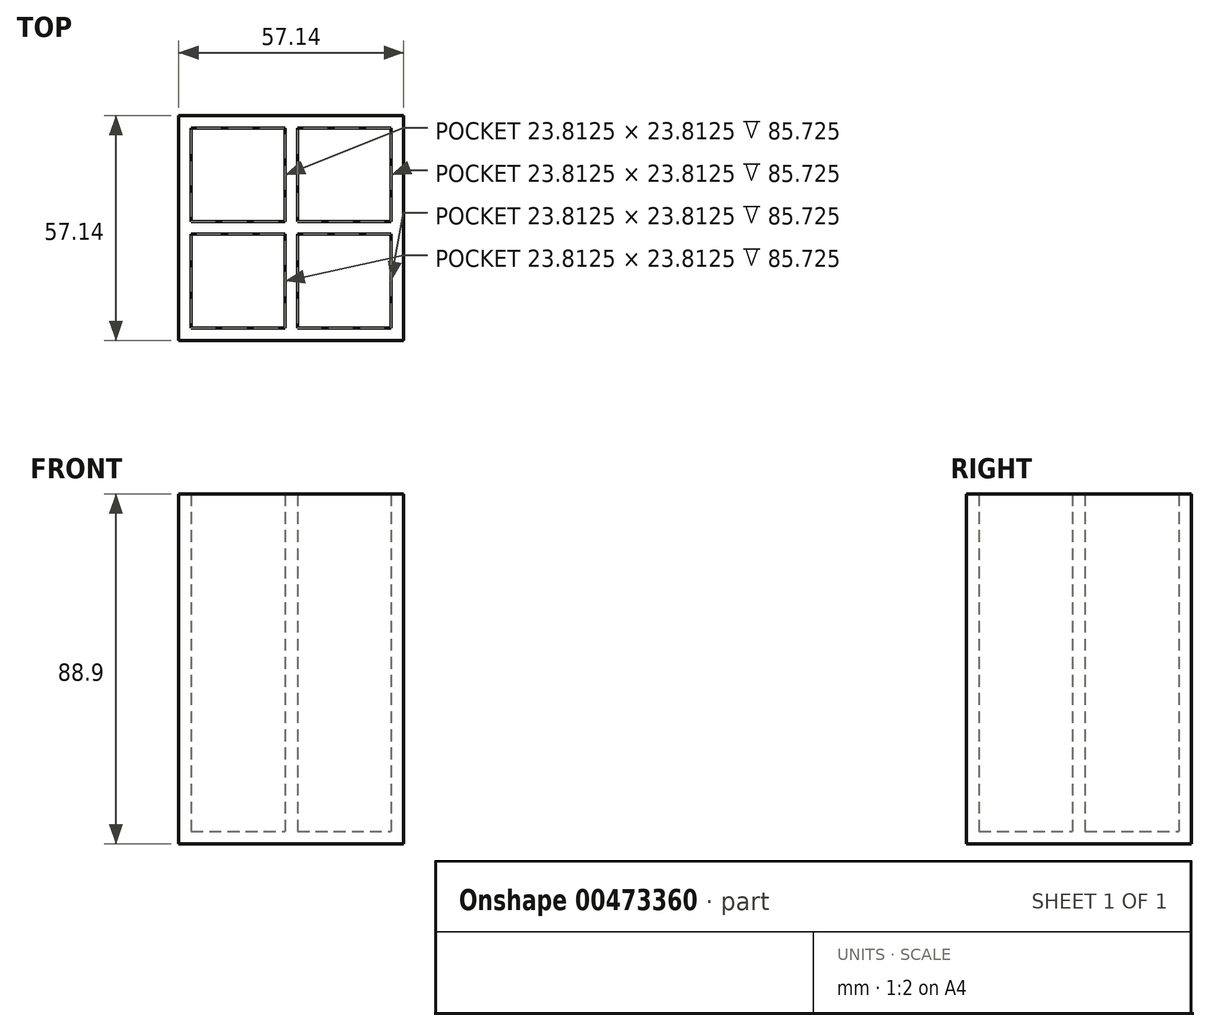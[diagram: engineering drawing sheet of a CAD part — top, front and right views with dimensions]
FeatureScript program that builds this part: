
annotation { "Feature Type Name" : "Feature", "Feature Type Description" : "" }
export const myFeature = defineFeature(function(context is Context, id is Id, definition is map)
    precondition{}
    {
        {
            var Q0;
            Q0=qCreatedBy(makeId("Top.planeOp"),FACE);
            var sketch = newSketch(context, id + "F0", { "sketchPlane" : qUnion([Q0])});
            skLineSegment(sketch, "E0.bottom", {"start": v(28.57, 28.58) * mm, "end": v(-28.58, 28.58) * mm});
            skLineSegment(sketch, "E0.top", {"start": v(28.57, -28.58) * mm, "end": v(-28.57, -28.58) * mm});
            skLineSegment(sketch, "E0.left", {"start": v(28.57, 28.58) * mm, "end": v(28.58, -28.57) * mm});
            skLineSegment(sketch, "E0.right", {"start": v(-28.58, 28.58) * mm, "end": v(-28.57, -28.57) * mm});
            skPoint(sketch, "E0.middle", {"position": v(0, 0) * mm});
            skSolve(sketch);
        }
        {
            var Q0;
            Q0=makeQuery(id+"F0.imprint","IMPRINT",FACE,{"disambiguationData":[TD([[makeQuery(id+"F0.imprint","IMPRINT",EDGE,{"derivedFrom":sQuery(id+"F0.wireOp",EDGE,"E0.bottom")}),1.0]])]});
            extrude(context, id + "F1", {"entities" : qUnion([Q0]), "depth" : 88.9 * mm});
        }
        {
            var Q0;
            Q0=makeQuery(id+"F1.opExtrude","CAP_FACE",FACE,{"disambiguationData":[OSD([sQuery(id+"F0.wireOp",EDGE,"E0.bottom"),sQuery(id+"F0.wireOp",EDGE,"E0.top"),sQuery(id+"F0.wireOp",EDGE,"E0.left"),sQuery(id+"F0.wireOp",EDGE,"E0.right")])],"isStart":true});
            var sketch = newSketch(context, id + "F2", { "sketchPlane" : qUnion([Q0])});
            skLineSegment(sketch, "E1.bottom", {"start": v(25.4, 25.4) * mm, "end": v(1.59, 25.4) * mm});
            skLineSegment(sketch, "E1.top", {"start": v(25.4, 1.59) * mm, "end": v(1.59, 1.59) * mm});
            skLineSegment(sketch, "E1.left", {"start": v(25.4, 25.4) * mm, "end": v(25.4, 1.59) * mm});
            skLineSegment(sketch, "E1.right", {"start": v(1.59, 25.4) * mm, "end": v(1.59, 1.59) * mm});
            skPoint(sketch, "E1.middle", {"position": v(13.5, 13.5) * mm});
            skLineSegment(sketch, "E2.bottom", {"start": v(25.4, -25.4) * mm, "end": v(1.59, -25.4) * mm});
            skLineSegment(sketch, "E2.top", {"start": v(25.4, -1.59) * mm, "end": v(1.59, -1.59) * mm});
            skLineSegment(sketch, "E2.left", {"start": v(25.4, -25.4) * mm, "end": v(25.4, -1.59) * mm});
            skLineSegment(sketch, "E2.right", {"start": v(1.59, -25.4) * mm, "end": v(1.59, -1.59) * mm});
            skPoint(sketch, "E2.middle", {"position": v(13.5, -13.5) * mm});
            skLineSegment(sketch, "E3.bottom", {"start": v(-1.59, -25.4) * mm, "end": v(-25.4, -25.4) * mm});
            skLineSegment(sketch, "E3.top", {"start": v(-1.59, -1.59) * mm, "end": v(-25.4, -1.59) * mm});
            skLineSegment(sketch, "E3.left", {"start": v(-1.59, -25.4) * mm, "end": v(-1.59, -1.59) * mm});
            skLineSegment(sketch, "E3.right", {"start": v(-25.4, -25.4) * mm, "end": v(-25.4, -1.59) * mm});
            skPoint(sketch, "E3.middle", {"position": v(-13.5, -13.5) * mm});
            skLineSegment(sketch, "E4.bottom", {"start": v(-1.59, 1.59) * mm, "end": v(-25.4, 1.59) * mm});
            skLineSegment(sketch, "E4.top", {"start": v(-1.59, 25.4) * mm, "end": v(-25.4, 25.4) * mm});
            skLineSegment(sketch, "E4.left", {"start": v(-1.59, 1.59) * mm, "end": v(-1.59, 25.4) * mm});
            skLineSegment(sketch, "E4.right", {"start": v(-25.4, 1.59) * mm, "end": v(-25.4, 25.4) * mm});
            skPoint(sketch, "E4.middle", {"position": v(-13.5, 13.5) * mm});
            skSolve(sketch);
        }
        {
            var Q0;
            Q0=makeQuery(id+"F2.imprint","IMPRINT",FACE,{"disambiguationData":[TD([[makeQuery(id+"F2.imprint","IMPRINT",EDGE,{"derivedFrom":sQuery(id+"F2.wireOp",EDGE,"E4.bottom")}),-1.0]])]});
            var Q1;
            Q1=makeQuery(id+"F2.imprint","IMPRINT",FACE,{"disambiguationData":[TD([[makeQuery(id+"F2.imprint","IMPRINT",EDGE,{"derivedFrom":sQuery(id+"F2.wireOp",EDGE,"E1.bottom")}),1.0]])]});
            var Q2;
            Q2=makeQuery(id+"F2.imprint","IMPRINT",FACE,{"disambiguationData":[TD([[makeQuery(id+"F2.imprint","IMPRINT",EDGE,{"derivedFrom":sQuery(id+"F2.wireOp",EDGE,"E2.bottom")}),-1.0]])]});
            var Q3;
            Q3=makeQuery(id+"F2.imprint","IMPRINT",FACE,{"disambiguationData":[TD([[makeQuery(id+"F2.imprint","IMPRINT",EDGE,{"derivedFrom":sQuery(id+"F2.wireOp",EDGE,"E3.bottom")}),-1.0]])]});
            extrude(context, id + "F3", {"entities" : qUnion([Q0, Q1, Q2, Q3]), "operationType" : NewBodyOperationType.REMOVE, "oppositeDirection" : true, "depth" : 111.25 * mm});
        }
        {
            var Q0;
            Q0=makeQuery(id+"F1.opExtrude","CAP_FACE",FACE,{"disambiguationData":[OSD([sQuery(id+"F0.wireOp",EDGE,"E0.bottom"),sQuery(id+"F0.wireOp",EDGE,"E0.top"),sQuery(id+"F0.wireOp",EDGE,"E0.left"),sQuery(id+"F0.wireOp",EDGE,"E0.right")])],"isStart":true});
            var sketch = newSketch(context, id + "F4", { "sketchPlane" : qUnion([Q0])});
            skLineSegment(sketch, "E5.bottom", {"start": v(-28.57, 28.57) * mm, "end": v(28.57, 28.57) * mm});
            skLineSegment(sketch, "E5.top", {"start": v(-28.57, -28.58) * mm, "end": v(28.57, -28.58) * mm});
            skLineSegment(sketch, "E5.left", {"start": v(-28.57, 28.57) * mm, "end": v(-28.57, -28.58) * mm});
            skLineSegment(sketch, "E5.right", {"start": v(28.57, 28.57) * mm, "end": v(28.57, -28.58) * mm});
            skSolve(sketch);
        }
        {
            var Q0;
            Q0 = qSketchRegion(id + "F4", true);
            extrude(context, id + "F5", {"entities" : qUnion([Q0]), "operationType" : NewBodyOperationType.ADD, "oppositeDirection" : true, "depth" : 3.17 * mm});
        }
    });
